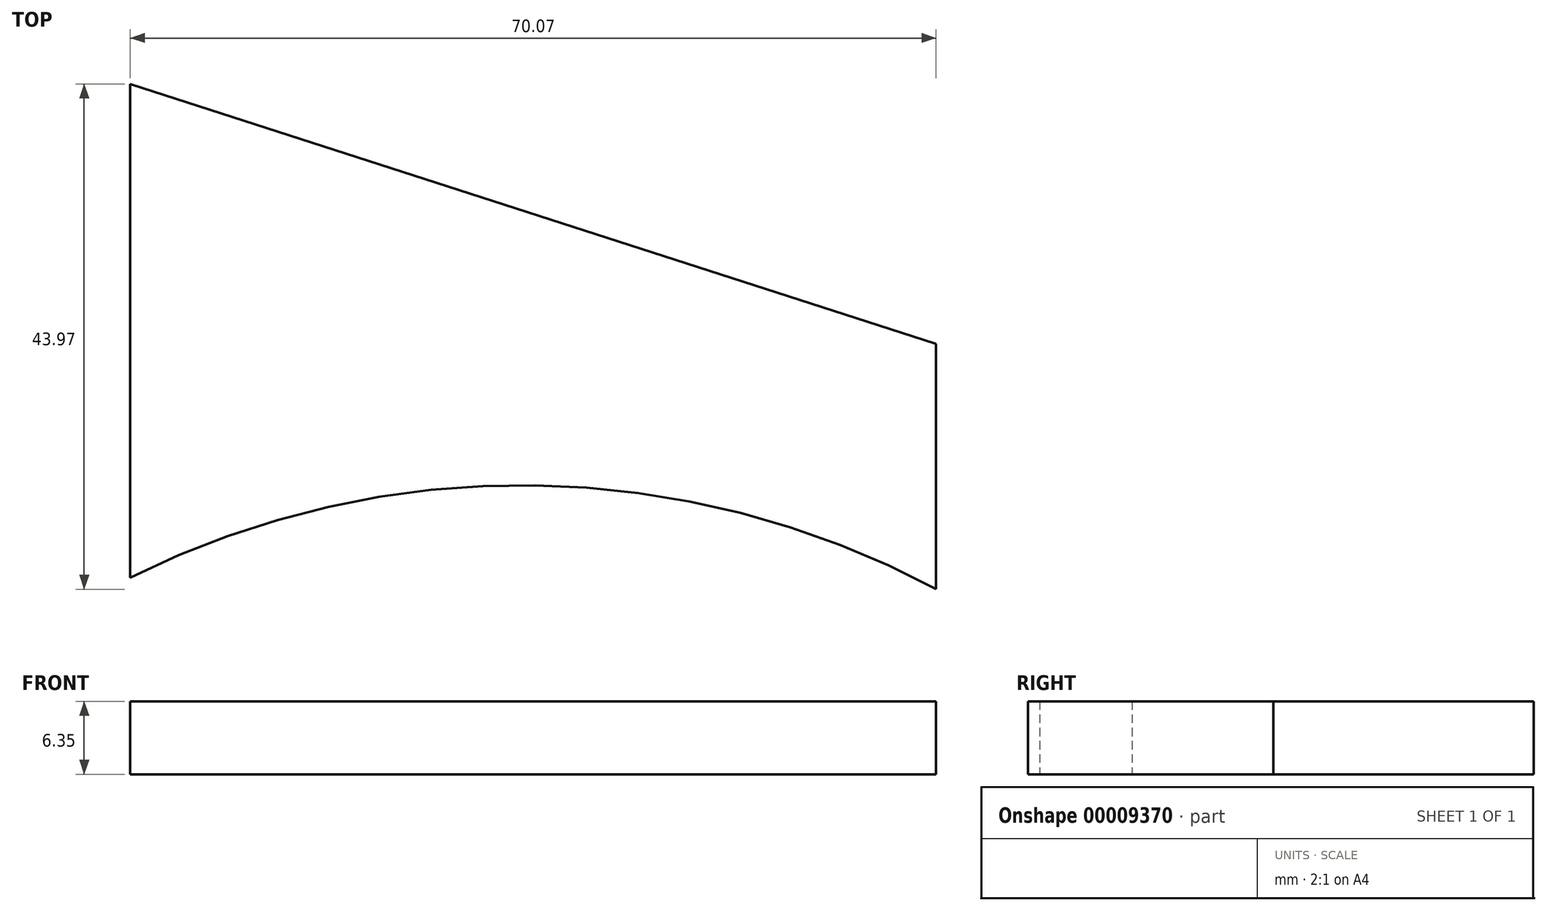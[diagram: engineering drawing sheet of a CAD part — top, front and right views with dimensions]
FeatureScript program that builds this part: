
annotation { "Feature Type Name" : "Feature", "Feature Type Description" : "" }
export const myFeature = defineFeature(function(context is Context, id is Id, definition is map)
    precondition{}
    {
        {
            var Q0;
            Q0=qCreatedBy(makeId("Top.planeOp"),FACE);
            var sketch = newSketch(context, id + "F0", { "sketchPlane" : qUnion([Q0])});
            skCircle(sketch, "E0", {"center": v(0, 0) * mm, "radius": 76.2 * mm});
            skCircle(sketch, "E1", {"center": v(0, 0) * mm, "radius": 101.6 * mm});
            skLineSegment(sketch, "E2", {"start": v(0, 0) * mm, "end": v(0, 101.6) * mm});
            skLineSegment(sketch, "E3", {"start": v(36, 67.15) * mm, "end": v(36, 88.5) * mm});
            skLineSegment(sketch, "E4", {"start": v(36, 88.5) * mm, "end": v(-34.06, 111.12) * mm});
            skLineSegment(sketch, "E5", {"start": v(-34.06, 111.12) * mm, "end": v(-34.06, 68.17) * mm});
            skSolve(sketch);
        }
        {
            var Q0;
            {var subQ0=sQuery(id+"F0.wireOp",EDGE,"E5");var subQ3=sQuery(id+"F0.wireOp",EDGE,"E0");var subQ4=makeQuery(id+"F0.imprint","INTERSECT",VERTEX,{"derivedFrom":[subQ3,subQ0]});Q0=makeQuery(id+"F0.imprint","IMPRINT",FACE,{"disambiguationData":[TD([[makeQuery(id+"F0.imprint","IMPRINT",EDGE,{"disambiguationData":[TD([[subQ4,1.0]])],"derivedFrom":subQ3}),-1.0]])]});}
            var Q1;
            {var subQ1=sQuery(id+"F0.wireOp",EDGE,"E1");var subQ3=sQuery(id+"F0.wireOp",EDGE,"E4");var subQ5=makeQuery(id+"F0.imprint","INTERSECT",VERTEX,{"derivedFrom":[subQ1,subQ3]});Q1=makeQuery(id+"F0.imprint","IMPRINT",FACE,{"disambiguationData":[TD([[makeQuery(id+"F0.imprint","IMPRINT",EDGE,{"disambiguationData":[TD([[subQ5,-1.0]])],"derivedFrom":subQ1}),-1.0]])]});}
            var Q2;
            {var subQ3=sQuery(id+"F0.wireOp",EDGE,"E3");Q2=makeQuery(id+"F0.imprint","IMPRINT",FACE,{"disambiguationData":[TD([[makeQuery(id+"F0.imprint","IMPRINT",EDGE,{"derivedFrom":subQ3}),1.0]])]});}
            extrude(context, id + "F1", {"entities" : qUnion([Q0, Q1, Q2]), "depth" : 6.35 * mm});
        }
    });
